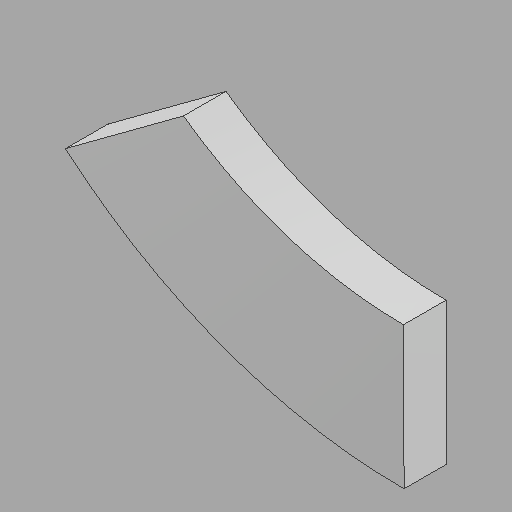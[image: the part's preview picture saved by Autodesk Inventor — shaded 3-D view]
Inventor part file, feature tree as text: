
AUTODESK INVENTOR PART (.ipt)
format: ipt  version: 2022.1 (Build 261234020, 234B)  size: 89,600 bytes
history: imported  units: in
note: dims shown in document units (in); Inventor stores cm internally (conversion verified against a paired STEP export)
features: imported_body x1
ambient origin geometry x8: Origin, YZ Plane, XZ Plane, XY Plane, X Axis, Y Axis, Z Axis, Center Point
bodies: Solid1 (imported_parasolid)
feature tree (1):
  imported_body  NMx_Import_Brep_tag  [imported B-rep: ~6 faces, bbox_mm=[1213.186396, 761.386567, 152.4]]
